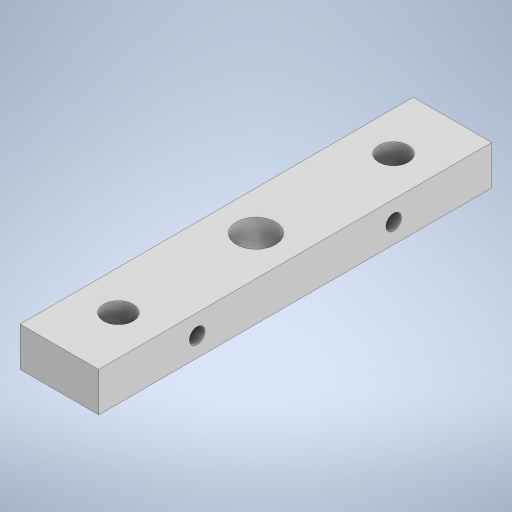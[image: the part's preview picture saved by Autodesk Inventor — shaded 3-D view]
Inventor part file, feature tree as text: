
AUTODESK INVENTOR PART (.ipt)
format: ipt  version: 2024 (Build 280153000, 153)  size: 242,176 bytes
history: native  units: mm
features: extrude x3
ambient origin geometry x8: Origin, YZ Plane, XZ Plane, XY Plane, X Axis, Y Axis, Z Axis, Center Point
bodies: Solid1 (feature_tree)
feature tree (3):
  extrude  "Extrusion1"  Depth=25.4mm
  extrude  "Extrusion2"  Depth=50.8mm
  extrude  "Extrusion3"  Depth=254.0mm TaperAngle=0.0deg
